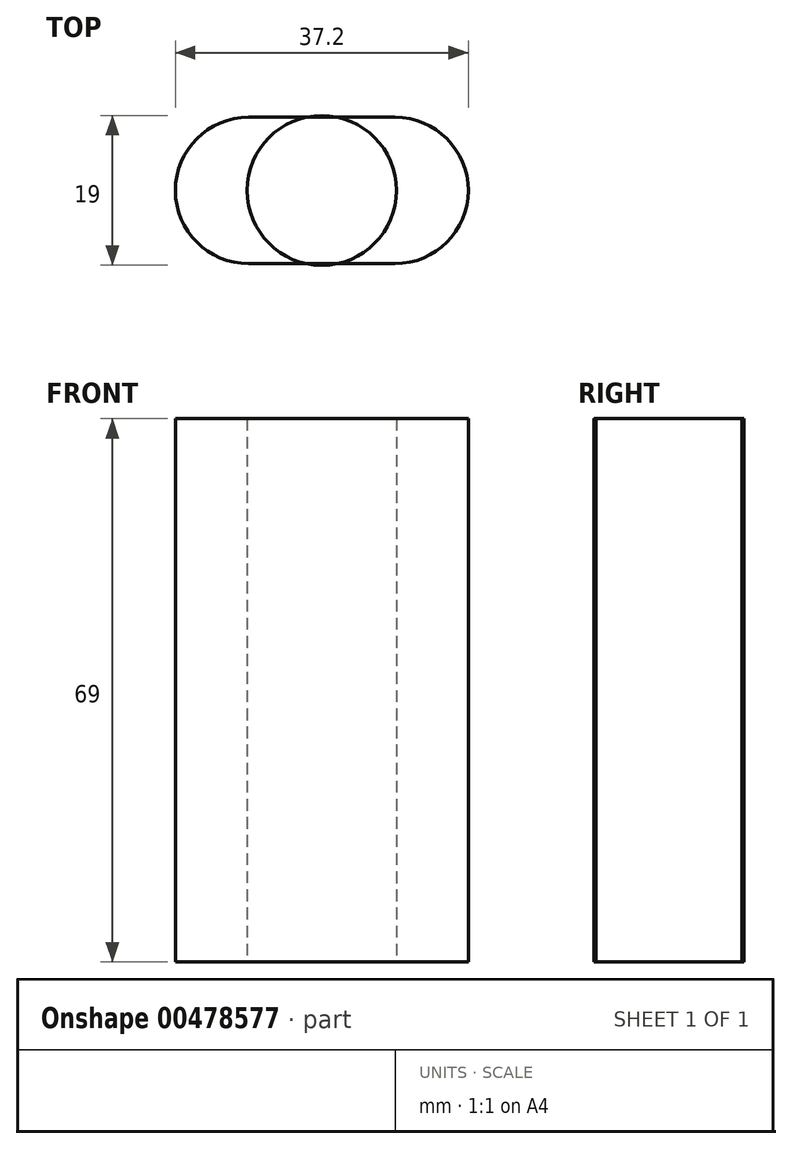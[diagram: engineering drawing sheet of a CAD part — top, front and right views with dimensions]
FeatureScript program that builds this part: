
annotation { "Feature Type Name" : "Feature", "Feature Type Description" : "" }
export const myFeature = defineFeature(function(context is Context, id is Id, definition is map)
    precondition{}
    {
        {
            var Q0;
            Q0=qCreatedBy(makeId("Top.planeOp"),FACE);
            var sketch = newSketch(context, id + "F0", { "sketchPlane" : qUnion([Q0])});
            skCircle(sketch, "E0", {"center": v(9.3, 0) * mm, "radius": 9.3 * mm});
            skLineSegment(sketch, "E1", {"start": v(0, 0) * mm, "end": v(0, 27.23) * mm, "construction": true});
            skCircle(sketch, "E2.MirrorC", {"center": v(-9.3, 0) * mm, "radius": 9.3 * mm});
            skLineSegment(sketch, "E3", {"start": v(-9.3, 9.3) * mm, "end": v(9.3, 9.3) * mm});
            skLineSegment(sketch, "E4", {"start": v(-9.3, 9.3) * mm, "end": v(-9.3, 0) * mm, "construction": true});
            skLineSegment(sketch, "E5", {"start": v(-9.3, -9.3) * mm, "end": v(9.3, -9.3) * mm});
            skLineSegment(sketch, "E6", {"start": v(-9.3, -9.3) * mm, "end": v(-9.3, 0) * mm, "construction": true});
            skSolve(sketch);
        }
        {
            var Q0;
            Q0 = qSketchRegion(id + "F0", true);
            extrude(context, id + "F1", {"entities" : qUnion([Q0]), "depth" : 69 * mm});
        }
        {
            var Q0;
            Q0=qCreatedBy(makeId("Top.planeOp"),FACE);
            var sketch = newSketch(context, id + "F2", { "sketchPlane" : qUnion([Q0])});
            skCircle(sketch, "E7", {"center": v(0, 0) * mm, "radius": 9.5 * mm});
            skSolve(sketch);
        }
        {
            var Q0;
            Q0 = qSketchRegion(id + "F2", true);
            extrude(context, id + "F3", {"entities" : qUnion([Q0]), "depth" : 69 * mm});
        }
    });
